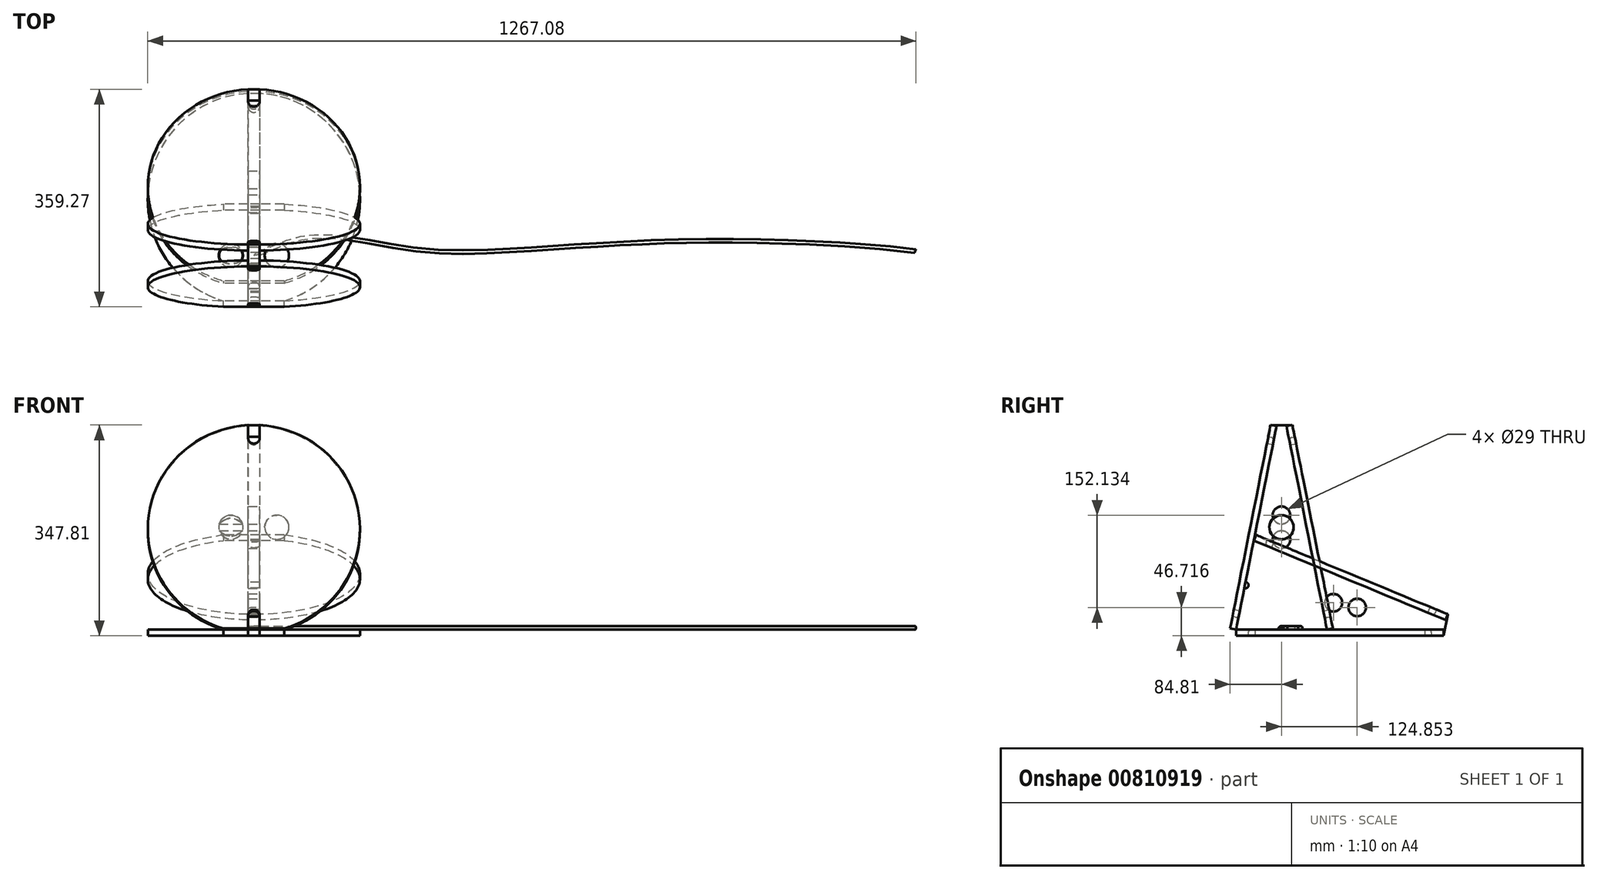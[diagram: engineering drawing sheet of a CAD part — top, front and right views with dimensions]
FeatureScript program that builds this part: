
annotation { "Feature Type Name" : "Feature", "Feature Type Description" : "" }
export const myFeature = defineFeature(function(context is Context, id is Id, definition is map)
    precondition{}
    {
        {
            var Q0;
            Q0=qCreatedBy(makeId("Front.planeOp"),FACE);
            var Q1;
            Q1=qCreatedBy(makeId("Top.planeOp"),FACE);
            cPlane(context, id + "F0", {"entities" : qUnion([Q0, Q1]), "cplaneType" : CPlaneType.MID_PLANE, "offset" : 25.4 * mm, "flipAlignment" : true, "width" : 152.4 * mm, "height" : 152.4 * mm});
        }
        {
            var Q0;
            Q0=qCreatedBy(id+"F0.planeOp",FACE);
            var Q1;
            Q1=qCreatedBy(makeId("Front.planeOp"),FACE);
            cPlane(context, id + "F1", {"entities" : qUnion([Q0, Q1]), "cplaneType" : CPlaneType.MID_PLANE, "offset" : 25.4 * mm, "flipAlignment" : true, "width" : 152.4 * mm, "height" : 152.4 * mm});
        }
        {
            var Q0;
            Q0=qCreatedBy(id+"F1.planeOp",FACE);
            var Q1;
            Q1=qCreatedBy(makeId("Front.planeOp"),FACE);
            cPlane(context, id + "F2", {"entities" : qUnion([Q0, Q1]), "cplaneType" : CPlaneType.MID_PLANE, "offset" : 25.4 * mm, "flipAlignment" : true, "width" : 152.4 * mm, "height" : 152.4 * mm});
        }
        {
            var Q0;
            Q0=qCreatedBy(id+"F2.planeOp",FACE);
            var sketch = newSketch(context, id + "F3", { "sketchPlane" : qUnion([Q0])});
            skArc(sketch, "E0", {"start": v(50, 0) * mm, "mid": v(0, 342.7) * mm, "end": v(-50, 0) * mm});
            skLineSegment(sketch, "E1", {"start": v(50, 0) * mm, "end": v(-50, 0) * mm});
            skSolve(sketch);
        }
        {
            var Q0;
            Q0=qSketchRegion(id+"F3",true);
            extrude(context, id + "F4", {"entities" : qUnion([Q0]), "depth" : 10 * mm, "offsetDistance" : 25 * mm});
        }
        {
            var Q0;
            Q0=qCreatedBy(makeId("Front.planeOp"),FACE);
            cPlane(context, id + "F5", {"entities" : qUnion([Q0]), "cplaneType" : CPlaneType.OFFSET, "offset" : 75 * mm, "oppositeDirection" : true, "width" : 150 * mm, "height" : 150 * mm});
        }
        {
            var Q0;
            Q0=makeQuery(id+"F4.opExtrude","CAP_FACE",FACE,{"disambiguationData":[OSD([sQuery(id+"F3.wireOp",EDGE,"E0"),sQuery(id+"F3.wireOp",EDGE,"E1")])],"isStart":false});
            var sketch = newSketch(context, id + "F6", { "sketchPlane" : qUnion([Q0])});
            skLineSegment(sketch, "E2.bottom", {"start": v(-9.6, -22) * mm, "end": v(9.6, -22) * mm});
            skLineSegment(sketch, "E2.left", {"start": v(-9.6, -22) * mm, "end": v(-9.6, 22) * mm});
            skLineSegment(sketch, "E2.right", {"start": v(9.6, -22) * mm, "end": v(9.6, 22) * mm});
            skPoint(sketch, "E2.middle", {"position": v(0, 0) * mm});
            skLineSegment(sketch, "E3.top", {"start": v(-9.6, 364.7) * mm, "end": v(9.6, 364.7) * mm});
            skLineSegment(sketch, "E3.left", {"start": v(-9.6, 320.7) * mm, "end": v(-9.6, 364.7) * mm});
            skLineSegment(sketch, "E3.right", {"start": v(9.6, 320.7) * mm, "end": v(9.6, 364.7) * mm});
            skPoint(sketch, "E3.middle", {"position": v(0, 342.7) * mm});
            skArc(sketch, "E4", {"start": v(9.6, 22) * mm, "mid": v(0, 31.6) * mm, "end": v(-9.6, 22) * mm});
            skArc(sketch, "E5", {"start": v(-9.6, 320.7) * mm, "mid": v(0, 311.1) * mm, "end": v(9.6, 320.7) * mm});
            skSolve(sketch);
        }
        {
            var Q0;
            Q0=qSketchRegion(id+"F6",true);
            extrude(context, id + "F7", {"entities" : qUnion([Q0]), "operationType" : NewBodyOperationType.REMOVE, "endBound" : BoundingType.THROUGH_ALL, "oppositeDirection" : true, "depth" : 25 * mm, "offsetDistance" : 25 * mm});
        }
        {
            var Q0;
            Q0=makeQuery(id+"F4.opExtrude","CAP_FACE",FACE,{"disambiguationData":[OSD([sQuery(id+"F3.wireOp",EDGE,"E0"),sQuery(id+"F3.wireOp",EDGE,"E1")])],"isStart":false});
            var sketch = newSketch(context, id + "F8", { "sketchPlane" : qUnion([Q0])});
            skArc(sketch, "E6.0", {"start": v(50, 0) * mm, "mid": v(173.8, 188.2) * mm, "end": v(9.6, 342.44) * mm});
            skLineSegment(sketch, "E6.1", {"start": v(50, 0) * mm, "end": v(9.6, 0) * mm});
            skLineSegment(sketch, "E7.1", {"start": v(-9.6, 0) * mm, "end": v(-9.6, 22) * mm});
            skLineSegment(sketch, "E7.2", {"start": v(9.6, 0) * mm, "end": v(9.6, 22) * mm});
            skPoint(sketch, "E7.3", {"position": v(0, 0) * mm});
            skLineSegment(sketch, "E7.5", {"start": v(-9.6, 320.7) * mm, "end": v(-9.6, 342.44) * mm});
            skLineSegment(sketch, "E7.6", {"start": v(9.6, 320.7) * mm, "end": v(9.6, 342.44) * mm});
            skPoint(sketch, "E7.7", {"position": v(0, 342.7) * mm});
            skArc(sketch, "E7.8", {"start": v(9.6, 22) * mm, "mid": v(0, 31.6) * mm, "end": v(-9.6, 22) * mm});
            skArc(sketch, "E7.9", {"start": v(-9.6, 320.7) * mm, "mid": v(0, 311.1) * mm, "end": v(9.6, 320.7) * mm});
            skPoint(sketch, "E7.4.end.orphan", {"position": v(9.6, 364.7) * mm});
            skPoint(sketch, "E7.4.start.orphan", {"position": v(-9.6, 364.7) * mm});
            skArc(sketch, "E8.trimOffspring", {"start": v(-9.6, 342.44) * mm, "mid": v(-173.8, 188.2) * mm, "end": v(-50, 0) * mm});
            skPoint(sketch, "E7.0.end.orphan", {"position": v(9.6, -22) * mm});
            skPoint(sketch, "E7.0.start.orphan", {"position": v(-9.6, -22) * mm});
            skLineSegment(sketch, "E9.trimOffspring", {"start": v(-9.6, 0) * mm, "end": v(-50, 0) * mm});
            skSolve(sketch);
        }
        {
            var Q0;
            Q0=makeQuery(id+"F4.opExtrude","SWEPT_BODY",BODY,{"disambiguationData":[OSD([sQuery(id+"F3.wireOp",EDGE,"E0"),sQuery(id+"F3.wireOp",EDGE,"E1")])]});
            var Q1;
            Q1=makeQuery(id+"F1jAScYJ9BiHF60_4.opExtrude","SWEPT_BODY",BODY,{"disambiguationData":[OSD([sQuery(id+"F8.wireOp",EDGE,"E6.0"),sQuery(id+"F8.wireOp",EDGE,"E6.1"),sQuery(id+"F8.wireOp",EDGE,"E7.1"),sQuery(id+"F8.wireOp",EDGE,"E7.2"),sQuery(id+"F8.wireOp",EDGE,"E7.5"),sQuery(id+"F8.wireOp",EDGE,"E7.6"),sQuery(id+"F8.wireOp",EDGE,"E7.8"),sQuery(id+"F8.wireOp",EDGE,"E7.9"),sQuery(id+"F8.wireOp",EDGE,"E8.trimOffspring"),sQuery(id+"F8.wireOp",EDGE,"E9.trimOffspring")])]});
            var Q2;
            Q2=makeQuery(id+"FZ6tUxqLbVE1ZoO_5.opPattern","COPY",BODY,{"derivedFrom":makeQuery(id+"F1jAScYJ9BiHF60_4.opExtrude","SWEPT_BODY",BODY,{"disambiguationData":[OSD([sQuery(id+"F8.wireOp",EDGE,"E6.0"),sQuery(id+"F8.wireOp",EDGE,"E6.1"),sQuery(id+"F8.wireOp",EDGE,"E7.1"),sQuery(id+"F8.wireOp",EDGE,"E7.2"),sQuery(id+"F8.wireOp",EDGE,"E7.5"),sQuery(id+"F8.wireOp",EDGE,"E7.6"),sQuery(id+"F8.wireOp",EDGE,"E7.8"),sQuery(id+"F8.wireOp",EDGE,"E7.9"),sQuery(id+"F8.wireOp",EDGE,"E8.trimOffspring"),sQuery(id+"F8.wireOp",EDGE,"E9.trimOffspring")])]}),"instanceName":"1"});
            var Q3;
            Q3=qCreatedBy(id+"F5.planeOp",FACE);
            mirror(context, id + "F9", {"entities" : qUnion([Q0, Q1, Q2]), "mirrorPlane" : qUnion([Q3])});
        }
        {
            var Q0;
            Q0=qCreatedBy(makeId("Right.planeOp"),FACE);
            var sketch = newSketch(context, id + "F10", { "sketchPlane" : qUnion([Q0])});
            skLineSegment(sketch, "E10", {"start": v(0, 0) * mm, "end": v(75, 0) * mm});
            skLineSegment(sketch, "E11", {"start": v(75, 0) * mm, "end": v(75, 337.7) * mm});
            skLineSegment(sketch, "E12", {"start": v(62.88, 316.13) * mm, "end": v(3.9, 19.62) * mm});
            skLineSegment(sketch, "E13", {"start": v(3.9, 19.62) * mm, "end": v(-5.9, 21.57) * mm});
            skLineSegment(sketch, "E14", {"start": v(-5.9, 21.57) * mm, "end": v(-9.8, 1.95) * mm});
            skLineSegment(sketch, "E15", {"start": v(-9.8, 1.95) * mm, "end": v(0, 0) * mm});
            skLineSegment(sketch, "E16", {"start": v(62.88, 316.13) * mm, "end": v(53.07, 318.08) * mm});
            skLineSegment(sketch, "E17", {"start": v(53.07, 318.08) * mm, "end": v(56.98, 337.7) * mm});
            skLineSegment(sketch, "E18", {"start": v(56.98, 337.7) * mm, "end": v(75, 337.7) * mm});
            skSolve(sketch);
        }
        {
            var Q0;
            Q0=qSketchRegion(id+"F10",true);
            extrude(context, id + "F11", {"entities" : qUnion([Q0]), "depth" : (19 / 2) * mm, "offsetDistance" : 25 * mm, "hasSecondDirection" : true, "secondDirectionOppositeDirection" : true, "secondDirectionDepth" : (19 / 2) * mm});
        }
        {
            var Q0;
            Q0=makeQuery(id+"F11.opExtrude","SWEPT_BODY",BODY,{"disambiguationData":[OSD([sQuery(id+"F10.wireOp",EDGE,"E10"),sQuery(id+"F10.wireOp",EDGE,"E11"),sQuery(id+"F10.wireOp",EDGE,"E12"),sQuery(id+"F10.wireOp",EDGE,"E13"),sQuery(id+"F10.wireOp",EDGE,"E14"),sQuery(id+"F10.wireOp",EDGE,"E15"),sQuery(id+"F10.wireOp",EDGE,"E16"),sQuery(id+"F10.wireOp",EDGE,"E17"),sQuery(id+"F10.wireOp",EDGE,"E18")])]});
            var Q1;
            Q1=qCreatedBy(id+"F5.planeOp",FACE);
            mirror(context, id + "F12", {"operationType" : NewBodyOperationType.ADD, "entities" : qUnion([Q0]), "mirrorPlane" : qUnion([Q1])});
        }
        {
            var Q0;
            Q0=qCreatedBy(makeId("Top.planeOp"),FACE);
            cPlane(context, id + "F13", {"entities" : qUnion([Q0]), "cplaneType" : CPlaneType.OFFSET, "offset" : 3 * mm, "width" : 150 * mm, "height" : 150 * mm});
        }
        {
            var Q0;
            Q0=qCreatedBy(id+"F13.planeOp",FACE);
            var sketch = newSketch(context, id + "F14", { "sketchPlane" : qUnion([Q0])});
            skFitSpline(sketch, "E19", {"points": [v(0, 75) * mm, v(84.05, 104.6) * mm, v(247.75, 87.31) * mm, v(416.38, 82.9) * mm, v(763.05, 99.39) * mm, v(1090.84, 82.03) * mm], "startDerivative": vector(418.66, 113.12) * mm, "endDerivative": vector(571.08, -92.4) * mm});
            skSolve(sketch);
        }
        {
            var Q0;
            Q0=qCreatedBy(makeId("Right.planeOp"),FACE);
            var sketch = newSketch(context, id + "F15", { "sketchPlane" : qUnion([Q0])});
            skCircle(sketch, "E20", {"center": v(75, 3) * mm, "radius": 3 * mm});
            skSolve(sketch);
        }
        {
            var Q0;
            Q0=qSketchRegion(id+"F15",true);
            var Q1;
            Q1=qConstructionFilter(qBodyType(qCreatedBy(id+"F14",EDGE),BodyType.WIRE),ConstructionObject.NO);
            sweep(context, id + "F16", {"profiles" : qUnion([Q0]), "path" : qUnion([Q1])});
        }
        {
            var Q0;
            Q0=qCreatedBy(id+"F5.planeOp",FACE);
            var sketch = newSketch(context, id + "F17", { "sketchPlane" : qUnion([Q0])});
            skArc(sketch, "E21", {"start": v(37.93, 189.08) * mm, "mid": v(17.85, 169.08) * mm, "end": v(37.93, 149.08) * mm});
            skLineSegment(sketch, "E22", {"start": v(37.93, 189.08) * mm, "end": v(37.93, 149.08) * mm});
            skSolve(sketch);
        }
        {
            var Q0;
            Q0=qSketchRegion(id+"F17",true);
            var Q1;
            Q1=sQuery(id+"F17.wireOp",EDGE,"E21");
            var Q2;
            Q2=sQuery(id+"F17.wireOp",EDGE,"E22");
            var Q3;
            Q3=sQuery(id+"F17.wireOp",EDGE,"E22");
            revolve(context, id + "F18", {"surfaceOperationType" : NewSurfaceOperationType.NEW, "entities" : qUnion([Q0]), "surfaceEntities" : qUnion([Q1, Q2]), "axis" : qUnion([Q3]), "revolveType" : RevolveType.FULL});
        }
        {
            var Q0;
            Q0=makeQuery(id+"F18.opRevolve","SWEPT_BODY",BODY,{"disambiguationData":[OSD([sQuery(id+"F17.wireOp",EDGE,"E21"),sQuery(id+"F17.wireOp",EDGE,"E22")])]});
            var Q1;
            Q1=qCreatedBy(makeId("Right.planeOp"),FACE);
            mirror(context, id + "F19", {"entities" : qUnion([Q0]), "mirrorPlane" : qUnion([Q1])});
        }
        {
            var Q0;
            Q0=makeQuery(id+"F11.opExtrude","SWEPT_EDGE",EDGE,{"disambiguationData":[OSD([sQuery(id+"F10.wireOp",EDGE,"E12"),sQuery(id+"F10.wireOp",EDGE,"E16")])]});
            var Q1;
            Q1=makeQuery(id+"F11.opExtrude","SWEPT_EDGE",EDGE,{"disambiguationData":[OSD([sQuery(id+"F10.wireOp",EDGE,"E12"),sQuery(id+"F10.wireOp",EDGE,"E13")])]});
            var Q2;
            Q2=makeQuery(id+"F12.opPattern","COPY",EDGE,{"derivedFrom":makeQuery(id+"F11.opExtrude","SWEPT_EDGE",EDGE,{"disambiguationData":[OSD([sQuery(id+"F10.wireOp",EDGE,"E12"),sQuery(id+"F10.wireOp",EDGE,"E13")])]}),"instanceName":"1"});
            var Q3;
            Q3=makeQuery(id+"F12.opPattern","COPY",EDGE,{"derivedFrom":makeQuery(id+"F11.opExtrude","SWEPT_EDGE",EDGE,{"disambiguationData":[OSD([sQuery(id+"F10.wireOp",EDGE,"E12"),sQuery(id+"F10.wireOp",EDGE,"E16")])]}),"instanceName":"1"});
            fillet(context, id + "F20", {"entities" : qUnion([Q0, Q1, Q2, Q3]), "radius" : 5 * mm, "tangentPropagation" : true, "allowEdgeOverflow" : false});
        }
        {
            var Q0;
            {var subQ0=makeQuery(id+"F11.opExtrude","CAP_FACE",FACE,{"disambiguationData":[OSD([sQuery(id+"F10.wireOp",EDGE,"E10"),sQuery(id+"F10.wireOp",EDGE,"E11"),sQuery(id+"F10.wireOp",EDGE,"E12"),sQuery(id+"F10.wireOp",EDGE,"E13"),sQuery(id+"F10.wireOp",EDGE,"E14"),sQuery(id+"F10.wireOp",EDGE,"E15"),sQuery(id+"F10.wireOp",EDGE,"E16"),sQuery(id+"F10.wireOp",EDGE,"E17"),sQuery(id+"F10.wireOp",EDGE,"E18")])],"isStart":false});Q0=makeQuery(id+"F12.boolean.opBoolean","MERGE",FACE,{"derivedFrom":[subQ0,makeQuery(id+"F12.opPattern","COPY",FACE,{"derivedFrom":subQ0,"instanceName":"1"})]});}
            var sketch = newSketch(context, id + "F21", { "sketchPlane" : qUnion([Q0])});
            skSolve(sketch);
        }
        {
            var Q0;
            {var subQ4=sQuery(id+"F10.wireOp",EDGE,"E14");var subQ16=makeQuery(id+"F11.opExtrude","CAP_EDGE",EDGE,{"disambiguationData":[OSD([subQ4])],"isStart":false});Q0=makeQuery(id+"F21.imprint","IMPRINT",FACE,{"disambiguationData":[TD([[makeQuery(id+"F21.imprint","IMPRINT",EDGE,{"derivedFrom":subQ16}),1.0]])]});}
            var sketch = newSketch(context, id + "F22", { "sketchPlane" : qUnion([Q0])});
            skCircle(sketch, "E23", {"center": v(75, 148.85) * mm, "radius": 14.5 * mm});
            skLineSegment(sketch, "E24", {"start": v(75, 148.85) * mm, "end": v(75, 337.7) * mm, "construction": true});
            skCircle(sketch, "E25", {"center": v(75, 188.85) * mm, "radius": 14.5 * mm});
            skCircle(sketch, "E26", {"center": v(75, 188.85) * mm, "radius": 17.5 * mm, "construction": true});
            skCircle(sketch, "E27", {"center": v(75, 148.85) * mm, "radius": 17.5 * mm, "construction": true});
            skCircle(sketch, "E28", {"center": v(75, 168.85) * mm, "radius": 5 * mm, "construction": true});
            skLineSegment(sketch, "E29", {"start": v(75, 148.85) * mm, "end": v(75, 0) * mm, "construction": true});
            skLineSegment(sketch, "E30.bottom", {"start": v(70, -6) * mm, "end": v(80, -6) * mm});
            skLineSegment(sketch, "E30.top", {"start": v(75, 6) * mm, "end": v(75, 6) * mm});
            skLineSegment(sketch, "E30.left", {"start": v(70, -6) * mm, "end": v(70, 1) * mm});
            skLineSegment(sketch, "E30.right", {"start": v(80, -6) * mm, "end": v(80, 1) * mm});
            skPoint(sketch, "E30.middle", {"position": v(75, 0) * mm});
            skPoint(sketch, "E31.visualSharp", {"position": v(70, 6) * mm});
            skArc(sketch, "E31.filletArc", {"start": v(75, 6) * mm, "mid": v(71.46, 4.54) * mm, "end": v(70, 1) * mm});
            skPoint(sketch, "E32.visualSharp", {"position": v(80, 6) * mm});
            skArc(sketch, "E32.filletArc", {"start": v(80, 1) * mm, "mid": v(78.54, 4.54) * mm, "end": v(75, 6) * mm});
            skLineSegment(sketch, "E33", {"start": v(75, 168.85) * mm, "end": v(33.59, 168.85) * mm, "construction": true});
            skLineSegment(sketch, "E34.left", {"start": v(36.1, 163.85) * mm, "end": v(38.05, 173.67) * mm});
            skSolve(sketch);
        }
        {
            var Q0;
            Q0 = qSketchRegion(id + "F22", true);
            extrude(context, id + "F23", {"entities" : qUnion([Q0]), "operationType" : NewBodyOperationType.REMOVE, "endBound" : BoundingType.THROUGH_ALL, "oppositeDirection" : true, "depth" : 25 * mm, "offsetDistance" : 25 * mm});
        }
        {
            var Q0;
            Q0=qCreatedBy(id+"F2.planeOp",FACE);
            var Q1;
            Q1=qCreatedBy(makeId("Top.planeOp"),FACE);
            cPlane(context, id + "F24", {"entities" : qUnion([Q0, Q1]), "cplaneType" : CPlaneType.MID_PLANE, "offset" : 25 * mm, "flipAlignment" : true, "width" : 150 * mm, "height" : 150 * mm});
        }
        {
            var Q0;
            Q0=makeQuery(id+"F4.opExtrude","SWEPT_BODY",BODY,{"disambiguationData":[OSD([sQuery(id+"F3.wireOp",EDGE,"E0"),sQuery(id+"F3.wireOp",EDGE,"E1")])]});
            var Q1;
            Q1=qCreatedBy(id+"F24.planeOp",FACE);
            mirror(context, id + "F25", {"entities" : qUnion([Q0]), "mirrorPlane" : qUnion([Q1])});
        }
    });
